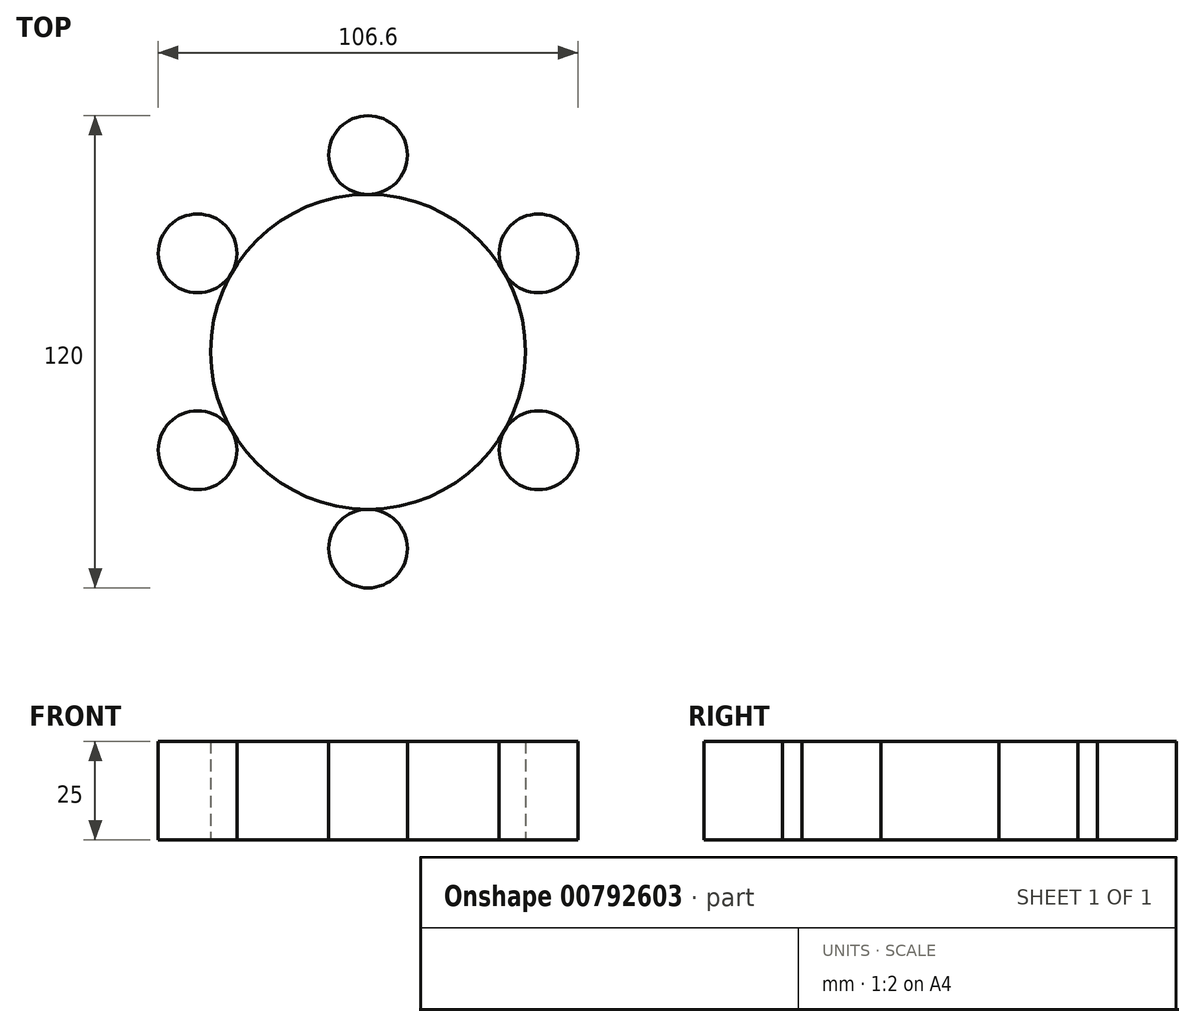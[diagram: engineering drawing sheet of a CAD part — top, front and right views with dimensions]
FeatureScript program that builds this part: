
annotation { "Feature Type Name" : "Feature", "Feature Type Description" : "" }
export const myFeature = defineFeature(function(context is Context, id is Id, definition is map)
    precondition{}
    {
        {
            var Q0;
            Q0=qCreatedBy(makeId("Top.planeOp"),FACE);
            var sketch = newSketch(context, id + "F0", { "sketchPlane" : qUnion([Q0])});
            skCircle(sketch, "E0", {"center": v(0, 0) * mm, "radius": 40 * mm});
            skCircle(sketch, "E1", {"center": v(0, 50) * mm, "radius": 10 * mm});
            skSolve(sketch);
        }
        {
            var Q0;
            Q0=makeQuery(id+"F0.imprint","IMPRINT",FACE,{"disambiguationData":[TD([[makeQuery(id+"F0.imprint","IMPRINT",EDGE,{"derivedFrom":sQuery(id+"F0.wireOp",EDGE,"E0")}),1.0]])]});
            extrude(context, id + "F1", {"entities" : qUnion([Q0]), "depth" : 25 * mm, "offsetDistance" : 25 * mm});
        }
        {
            var Q0;
            Q0=makeQuery(id+"F0.imprint","IMPRINT",FACE,{"disambiguationData":[TD([[makeQuery(id+"F0.imprint","IMPRINT",EDGE,{"derivedFrom":sQuery(id+"F0.wireOp",EDGE,"E1")}),1.0]])]});
            extrude(context, id + "F2", {"entities" : qUnion([Q0]), "depth" : 25 * mm, "offsetDistance" : 25 * mm});
        }
        {
            var Q0;
            Q0=makeQuery(id+"F2.opExtrude","SWEPT_BODY",BODY,{"disambiguationData":[OSD([sQuery(id+"F0.wireOp",EDGE,"E1")])]});
            var Q1;
            Q1=makeQuery(id+"F1.opExtrude","CAP_EDGE",EDGE,{"disambiguationData":[OSD([sQuery(id+"F0.wireOp",EDGE,"E0")])],"isStart":false});
            circularPattern(context, id + "F3", {"entities" : qUnion([Q0]), "axis" : qUnion([Q1]), "angle" : 360 * degree, "instanceCount" : 6, "equalSpace" : true});
        }
    });
